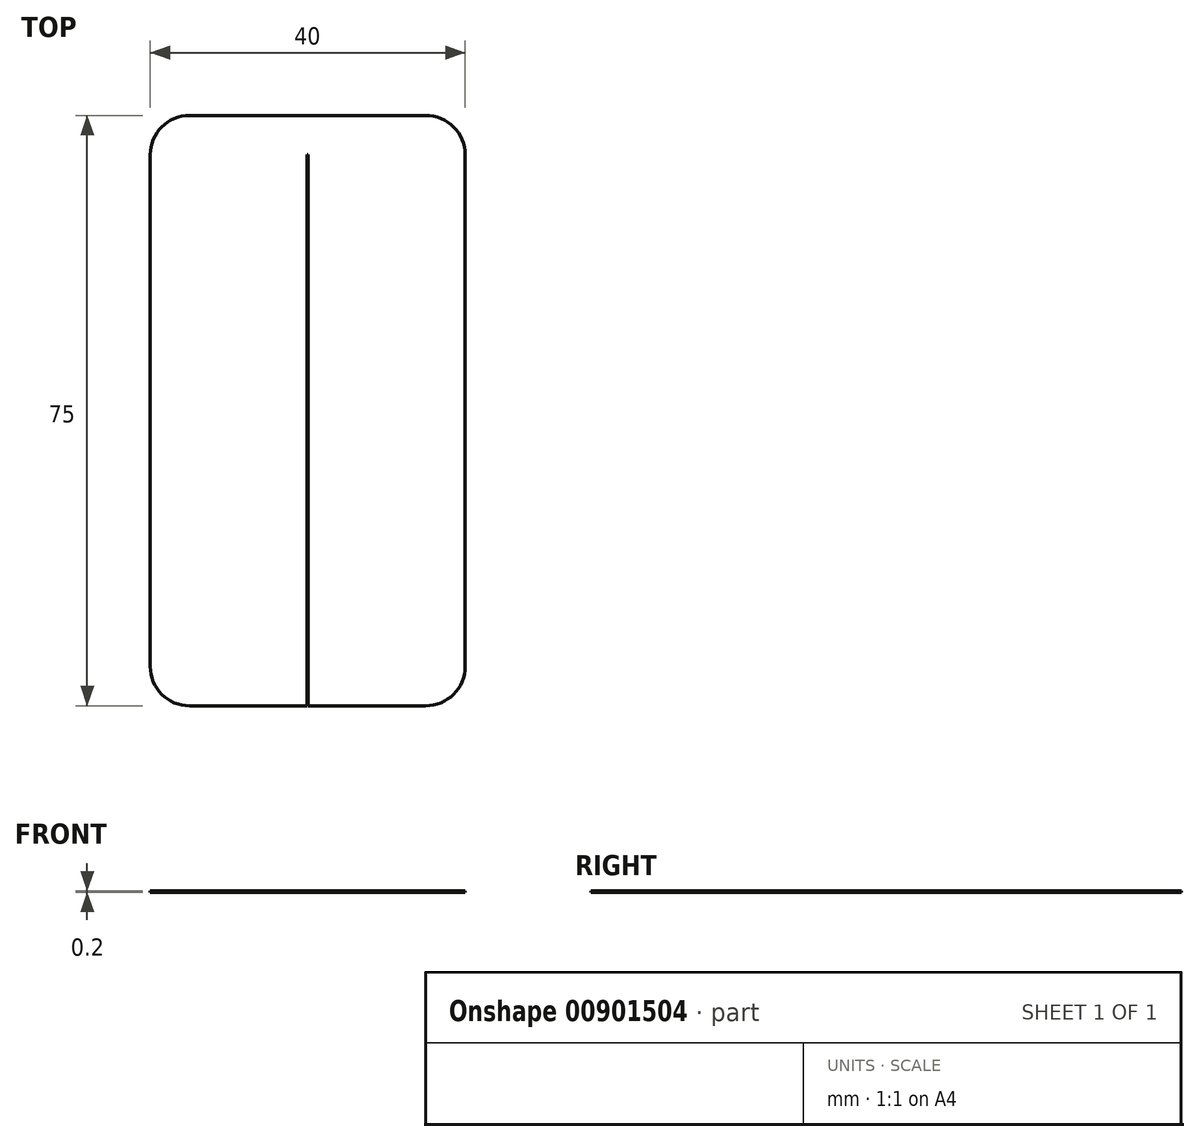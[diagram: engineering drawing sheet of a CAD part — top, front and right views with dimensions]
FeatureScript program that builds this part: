
annotation { "Feature Type Name" : "Feature", "Feature Type Description" : "" }
export const myFeature = defineFeature(function(context is Context, id is Id, definition is map)
    precondition{}
    {
        {
            var Q0;
            Q0=qCreatedBy(makeId("Top.planeOp"),FACE);
            var sketch = newSketch(context, id + "F0", { "sketchPlane" : qUnion([Q0])});
            skLineSegment(sketch, "E0.bottom", {"start": v(15, 37.5) * mm, "end": v(-15, 37.5) * mm});
            skLineSegment(sketch, "E0.top", {"start": v(15, -37.5) * mm, "end": v(-15, -37.5) * mm});
            skLineSegment(sketch, "E0.left", {"start": v(20, 32.5) * mm, "end": v(20, -32.5) * mm});
            skLineSegment(sketch, "E0.right", {"start": v(-20, 32.5) * mm, "end": v(-20, -32.5) * mm});
            skPoint(sketch, "E0.middle", {"position": v(0, 0) * mm});
            skLineSegment(sketch, "E1.bottom", {"start": v(-0.05, -37.5) * mm, "end": v(0.05, -37.5) * mm});
            skLineSegment(sketch, "E1.top", {"start": v(-0.05, 32.5) * mm, "end": v(0.05, 32.5) * mm});
            skLineSegment(sketch, "E1.left", {"start": v(-0.05, -37.5) * mm, "end": v(-0.05, 32.5) * mm});
            skLineSegment(sketch, "E1.right", {"start": v(0.05, -37.5) * mm, "end": v(0.05, 32.5) * mm});
            skLineSegment(sketch, "E2", {"start": v(0, -37.5) * mm, "end": v(0, 32.5) * mm, "construction": true});
            skPoint(sketch, "E3.visualSharp", {"position": v(-20, 37.5) * mm});
            skArc(sketch, "E3.filletArc", {"start": v(-15, 37.5) * mm, "mid": v(-18.54, 36.04) * mm, "end": v(-20, 32.5) * mm});
            skPoint(sketch, "E4.visualSharp", {"position": v(20, 37.5) * mm});
            skArc(sketch, "E4.filletArc", {"start": v(20, 32.5) * mm, "mid": v(18.54, 36.04) * mm, "end": v(15, 37.5) * mm});
            skPoint(sketch, "E5.visualSharp", {"position": v(20, -37.5) * mm});
            skArc(sketch, "E5.filletArc", {"start": v(15, -37.5) * mm, "mid": v(18.54, -36.04) * mm, "end": v(20, -32.5) * mm});
            skPoint(sketch, "E6.visualSharp", {"position": v(-20, -37.5) * mm});
            skArc(sketch, "E6.filletArc", {"start": v(-20, -32.5) * mm, "mid": v(-18.54, -36.04) * mm, "end": v(-15, -37.5) * mm});
            skSolve(sketch);
        }
        {
            var Q0;
            Q0=makeQuery(id+"F0.imprint","IMPRINT",FACE,{"disambiguationData":[TD([[makeQuery(id+"F0.imprint","IMPRINT",EDGE,{"derivedFrom":sQuery(id+"F0.wireOp",EDGE,"E0.bottom")}),1.0]])]});
            extrude(context, id + "F1", {"entities" : qUnion([Q0]), "depth" : .2 * mm, "offsetDistance" : 25 * mm});
        }
    });
